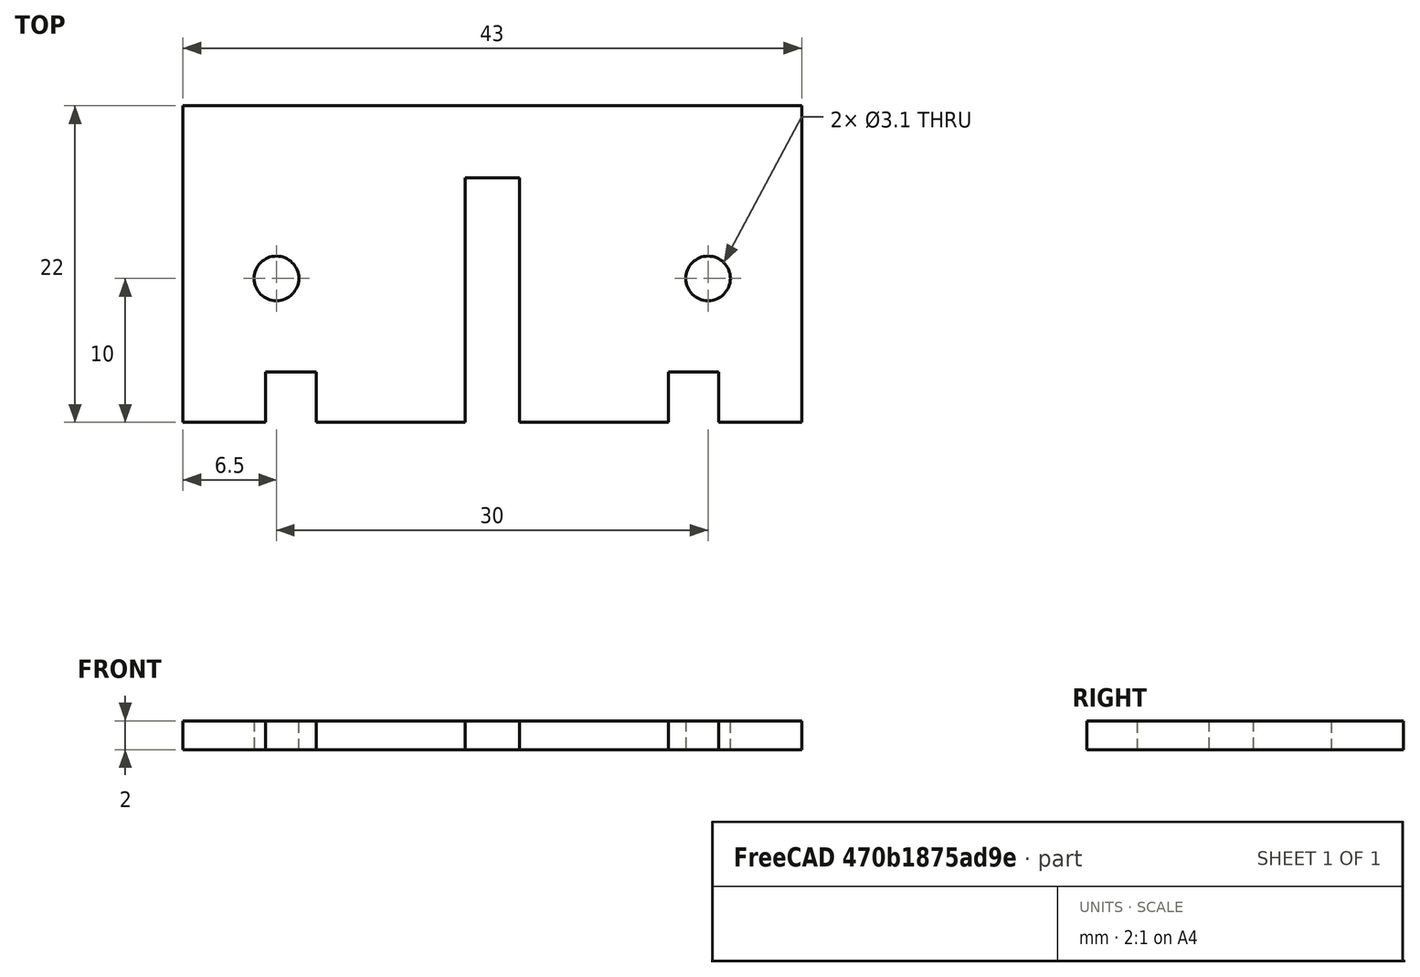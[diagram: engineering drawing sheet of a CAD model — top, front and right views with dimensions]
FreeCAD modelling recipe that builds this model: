
FCSTD DOCUMENT  (FreeCAD 1.0R)
Label: CW-Pad-Holder
License: All rights reserved
LicenseURL: https://en.wikipedia.org/wiki/All_rights_reserved
objects: Sketcher::SketchObject×1, PartDesign::Pad×1, PartDesign::Body×1, Part::Part2DObjectPython×1
note: 7 computed .brp shape members not serialized (recipe doc carries the construction recipe); baked Part::Feature solids carry a one-line shape summary decoded from their .brp

FEATURE [Sketcher::SketchObject] Sketch
  ArcFitTolerance = 1e-06
  FullyConstrained = true
  MakeInternals = false
  MapMode = 5
  sketch-geometry (23):
    g0: LineSegment StartX=21.5 StartY=-10 StartZ=0 EndX=21.5 EndY=12 EndZ=0
    g1: LineSegment StartX=21.5 StartY=12 StartZ=0 EndX=-21.5 EndY=12 EndZ=0
    g2: LineSegment StartX=-21.5 StartY=12 StartZ=0 EndX=-21.5 EndY=-10 EndZ=0
    g3: GeomPoint [constr] X=1e-16 Y=0 Z=0
    g4: LineSegment StartX=1.9 StartY=-10 StartZ=0 EndX=1.9 EndY=7 EndZ=0
    g5: LineSegment StartX=1.9 StartY=7 StartZ=0 EndX=-1.9 EndY=7 EndZ=0
    g6: LineSegment StartX=-1.9 StartY=7 StartZ=0 EndX=-1.9 EndY=-10 EndZ=0
    g7: GeomPoint [constr] X=0 Y=-1.5 Z=0
    g8: LineSegment [constr] StartX=15 StartY=12 StartZ=0 EndX=15 EndY=-10 EndZ=0
    g9: Circle CenterX=15 CenterY=0 CenterZ=0 NormalX=0 NormalY=0 NormalZ=1 AngleXU=0 Radius=1.55
    g10: Circle CenterX=-15 CenterY=0 CenterZ=0 NormalX=0 NormalY=0 NormalZ=1 AngleXU=0 Radius=1.55
    g11: LineSegment StartX=-12.25 StartY=-10 StartZ=0 EndX=-12.25 EndY=-6.5 EndZ=0
    g12: LineSegment StartX=-12.25 StartY=-6.5 StartZ=0 EndX=-15.75 EndY=-6.5 EndZ=0
    g13: LineSegment StartX=-15.75 StartY=-6.5 StartZ=0 EndX=-15.75 EndY=-10 EndZ=0
    g14: GeomPoint [constr] X=-14 Y=-8.25 Z=0
    g15: LineSegment StartX=-12.25 StartY=-10 StartZ=0 EndX=-1.9 EndY=-10 EndZ=0
    g16: LineSegment StartX=-21.5 StartY=-10 StartZ=0 EndX=-15.75 EndY=-10 EndZ=0
    g17: LineSegment StartX=15.75 StartY=-10 StartZ=0 EndX=15.75 EndY=-6.5 EndZ=0
    g18: LineSegment StartX=15.75 StartY=-6.5 StartZ=0 EndX=12.25 EndY=-6.5 EndZ=0
    g19: LineSegment StartX=12.25 StartY=-6.5 StartZ=0 EndX=12.25 EndY=-10 EndZ=0
    g20: GeomPoint [constr] X=14 Y=-8.25 Z=0
    g21: LineSegment StartX=15.75 StartY=-10 StartZ=0 EndX=21.5 EndY=-10 EndZ=0
    g22: LineSegment StartX=1.9 StartY=-10 StartZ=0 EndX=12.25 EndY=-10 EndZ=0
  constraints (60):
    c: Coincident(g21,g0)
    c: Coincident(g0,g1)
    c: Coincident(g1,g2)
    c: Coincident(g2,g16)
    c: Vertical(g0)
    c: Vertical(g2)
    c: Distance(g0,g2) = 43
    c: Distance(g16,g1) = 22
    c: Coincident(g3,g-1)
    c: Coincident(g4,g5)
    c: Coincident(g5,g6)
    c: Horizontal(g5)
    c: Vertical(g4)
    c: Vertical(g6)
    c: Symmetric(g5,g6,g7)
    c: Distance(g4,g6) = 3.8
    c: PointOnObject(g7,g-2)
    c: Horizontal(g4,g21)
    c: Coincident(g4,g22)
    c: Coincident(g6,g15)
    c: Horizontal(g4,g15)
    c: DistanceY(g5,g1) = 5
    c: DistanceY(g3,g0) = 12
    c: PointOnObject(g8,g1)
    c: Vertical(g8)
    c: Diameter(g9) = 3.1
    c: PointOnObject(g9,g8)
    c: PointOnObject(g9,g-1)
    c: Symmetric(g10,g9,g3)
    c: Equal(g10,g9)
    c: DistanceX(g3,g9) = 15
    c: Coincident(g11,g12)
    c: Coincident(g12,g13)
    c: Horizontal(g12)
    c: Vertical(g11)
    c: Vertical(g13)
    c: Symmetric(g12,g13,g14)
    c: Distance(g11,g13) = 3.5
    c: Distance(g13,g12) = 3.5
    c: Horizontal(g15)
    c: Horizontal(g16)
    c: Coincident(g16,g13)
    c: Coincident(g15,g11)
    c: Equal(g11,g13)
    c: Symmetric(g1,g0,g-2)
    c: Coincident(g17,g18)
    c: Coincident(g18,g19)
    c: Horizontal(g18)
    c: Vertical(g17)
    c: Vertical(g19)
    c: Symmetric(g18,g19,g20)
    c: Distance(g17,g19) = 3.5
    c: Distance(g19,g18) = 3.5
    c: PointOnObject(g8,g22)
    c: Coincident(g21,g17)
    c: Coincident(g19,g22)
    c: Parallel(g21,g1)
    c: Parallel(g22,g1)
    c: DistanceX(g14,g20) = 28
    c: Equal(g22,g15)
FEATURE [PartDesign::Pad] Pad
  Direction = (0,0,1)
  Length = 2
  Length2 = 10
  Midplane = true
  Profile = -> Sketch
  ReferenceAxis = -> Sketch [N_Axis]
  Refine = true
  Suppressed = false
  Type = 0
FEATURE [PartDesign::Body] Body
  AllowCompound = false
  Group = -> [Sketch,Pad]
  Origin = -> Origin
  Tip = -> Pad
FEATURE [Part::Part2DObjectPython] Shape2DView  # Draft 2D object (typed FeaturePython)
  AutoUpdate = true
  Base = -> Pad
  Clip = false
  FuseArch = false
  HiddenLines = false
  InPlace = true
  OnlySolids = false
  Projection = (0,0,1)
  ProjectionMode = 0
  SegmentLength = 0.05
  Tessellation = false
  VisibleOnly = false
